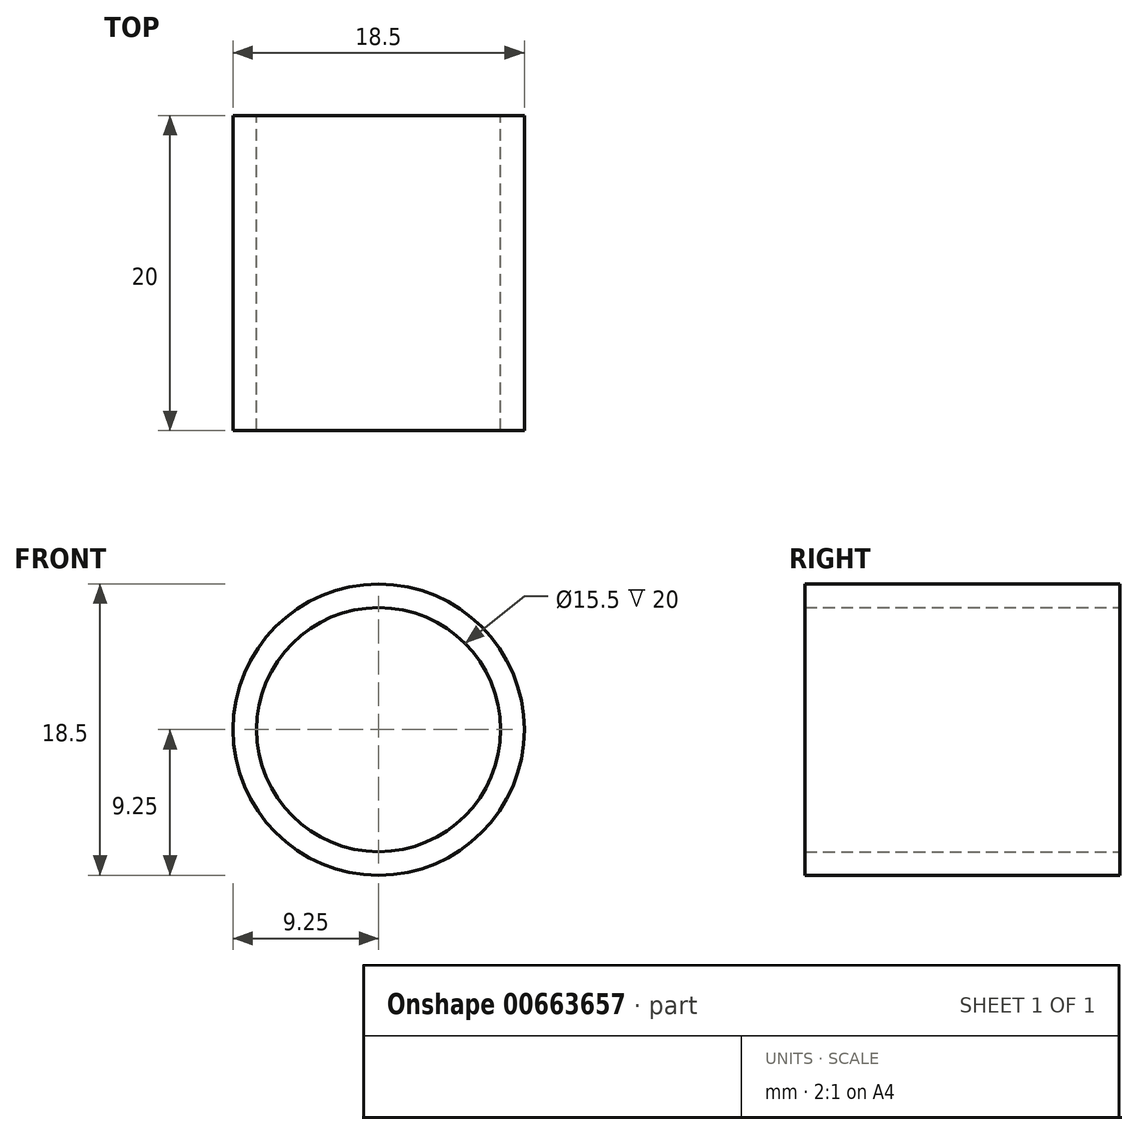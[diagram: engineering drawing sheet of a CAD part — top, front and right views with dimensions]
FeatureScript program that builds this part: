
annotation { "Feature Type Name" : "Feature", "Feature Type Description" : "" }
export const myFeature = defineFeature(function(context is Context, id is Id, definition is map)
    precondition{}
    {
        {
            var Q0;
            Q0=qCreatedBy(makeId("Front.planeOp"),FACE);
            var sketch = newSketch(context, id + "F0", { "sketchPlane" : qUnion([Q0])});
            skCircle(sketch, "E0", {"center": v(0, 0) * mm, "radius": 9.25 * mm});
            skCircle(sketch, "E1.0", {"center": v(0, 0) * mm, "radius": 7.75 * mm});
            skSolve(sketch);
        }
        {
            var Q0;
            Q0=qSketchRegion(id+"F0",true);
            extrude(context, id + "F1", {"entities" : qUnion([Q0]), "depth" : 20 * mm, "offsetDistance" : 25 * mm});
        }
    });
